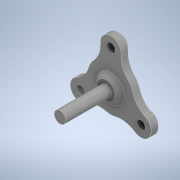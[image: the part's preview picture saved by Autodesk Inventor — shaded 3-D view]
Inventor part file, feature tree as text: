
AUTODESK INVENTOR PART (.ipt)
format: ipt  version: 2022 (Build 260153000, 153)  size: 160,256 bytes
history: mixed  units: in
note: dims shown in document units (in); Inventor stores cm internally (conversion verified against a paired STEP export)
features: extrude x1, sketch x1, chamfer x1, imported_body x1
ambient origin geometry x8: Origin, YZ Plane, XZ Plane, XY Plane, X Axis, Y Axis, Z Axis, Center Point
bodies: Solid1 (imported_parasolid)
feature tree (4):
  extrude  "Extrusion3"  [1 undecoded]
  sketch  "Sketch3"  dims[d4=0.7874in d5=0.0787in d6=0.0in d7=0.0in]
  chamfer  "Chamfer5"  [1 undecoded]
  imported_body  NMx_Import_Brep_tag  [imported B-rep: ~35 faces, bbox_mm=[31.788121, 26.496463, 26.0]]
note: 2 required parameter values undecoded (feature->parameter linkage not recoverable at this tier; creation-order binding heuristic only, values carry confidence <= 0.55)
